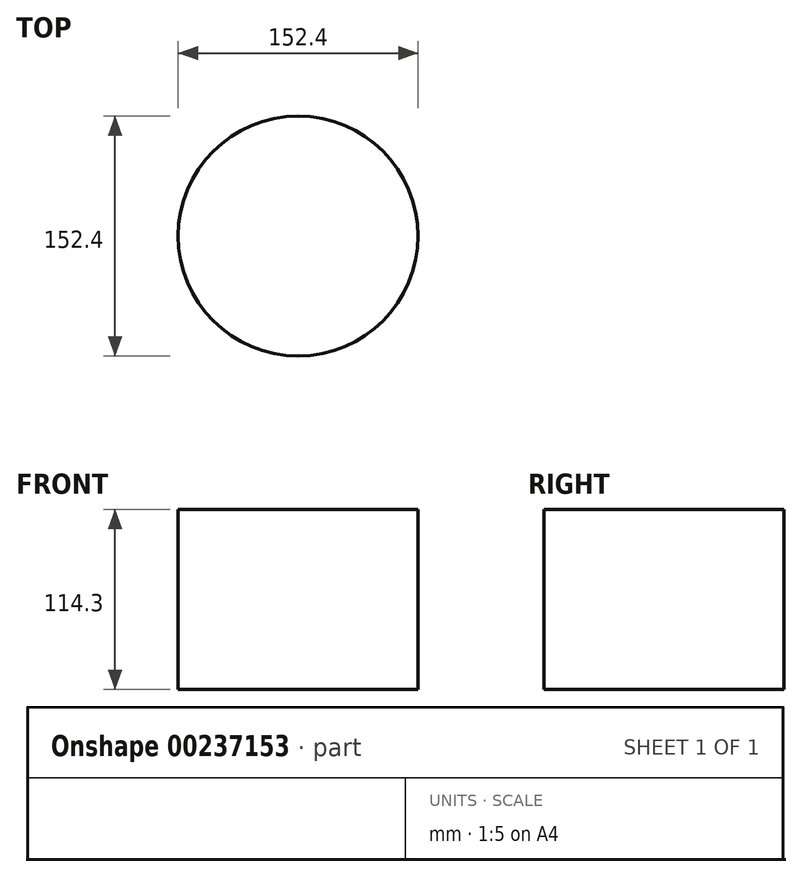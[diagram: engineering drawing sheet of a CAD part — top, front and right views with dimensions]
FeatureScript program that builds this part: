
annotation { "Feature Type Name" : "Feature", "Feature Type Description" : "" }
export const myFeature = defineFeature(function(context is Context, id is Id, definition is map)
    precondition{}
    {
        {
            var Q0;
            Q0=qCreatedBy(makeId("Top.planeOp"),FACE);
            var sketch = newSketch(context, id + "F0", { "sketchPlane" : qUnion([Q0])});
            skCircle(sketch, "E0", {"center": v(0, 0) * mm, "radius": 76.2 * mm});
            skSolve(sketch);
        }
        {
            var Q0;
            Q0=makeQuery(id+"F0.imprint","IMPRINT",FACE,{"disambiguationData":[TD([[makeQuery(id+"F0.imprint","IMPRINT",EDGE,{"derivedFrom":sQuery(id+"F0.wireOp",EDGE,"E0")}),1.0]])]});
            extrude(context, id + "F1", {"entities" : qUnion([Q0]), "depth" : 114.3 * mm});
        }
    });
